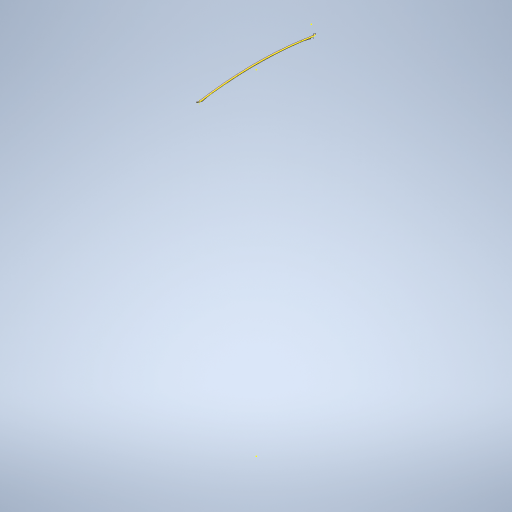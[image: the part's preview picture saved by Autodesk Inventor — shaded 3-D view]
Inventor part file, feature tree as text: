
AUTODESK INVENTOR PART (.ipt)
format: ipt  version: 2024.2 (Build 282272000, 272)  size: 412,160 bytes
history: native  units: mm
features: sketch x11, extrude x6
ambient origin geometry x8: Origin, YZ Plane, XZ Plane, XY Plane, X Axis, Y Axis, Z Axis, Center Point
bodies: Solid1 (feature_tree)
feature tree (17):
  extrude  "Extrusion1"  Depth=20000.0mm
  sketch  "Sketch2"  dims[d2=20000.0mm d3=0.0mm]
  sketch  "Sketch4"  dims[d4=0.0mm d5=2500.0mm]
  sketch  "Sketch5"  dims[d6=900.0mm d7=120.0mm]
  extrude  "Extrusion2"  TaperAngle=0.0deg  [1 undecoded]
  extrude  "Extrusion3"  Depth=2500.0mm
  extrude  "Extrusion4"  Depth=120.0mm
  sketch  "Sketch10"  dims[d13=120000.0mm]
  extrude  "Extrusion5"  TaperAngle=90.0deg  [1 undecoded]
  extrude  "Extrusion7"  Depth=200.0mm
  sketch  "Sketch13"  dims[d22=300.0mm d23=17500.0mm d24=90.0deg d25=17500.0mm d26=180.0deg d27=130000.0mm d28=300.0mm d29=0.0mm d30=29.670597mm d31=1.745329mm d32=1000.0mm d33=0.0mm d34=7000.0mm d35=90.0deg d36=3000.0mm d37=3000.0mm d38=6000.0mm d39=8000.0mm d40=3000.0mm d41=6000.0mm d42=100.0mm d43=200.0mm d44=100.0mm d45=200.0mm d46=100.0mm d47=200.0mm d48=300.0mm d49=0.0mm d53=35000.0mm d54=300.0mm d55=0.0mm]
  sketch  "Sketch1"  dims[d0=200000.0mm d1=20000.0mm]
  sketch  "Sketch7"  dims[d8=210.0mm d9=90.0deg]
  sketch  "Sketch8"  dims[d10=4000.0mm d11=200.0mm]
  sketch  "Sketch9"  dims[d12=60.0mm]
  sketch  "Sketch11"  dims[d14=150.0mm d15=150.0mm d16=0.0mm d17=0.0mm]
  sketch  "Sketch12"  dims[d20=300.0mm d21=0.0mm]
note: 2 required parameter values undecoded (feature->parameter linkage not recoverable at this tier; creation-order binding heuristic only, values carry confidence <= 0.55)
